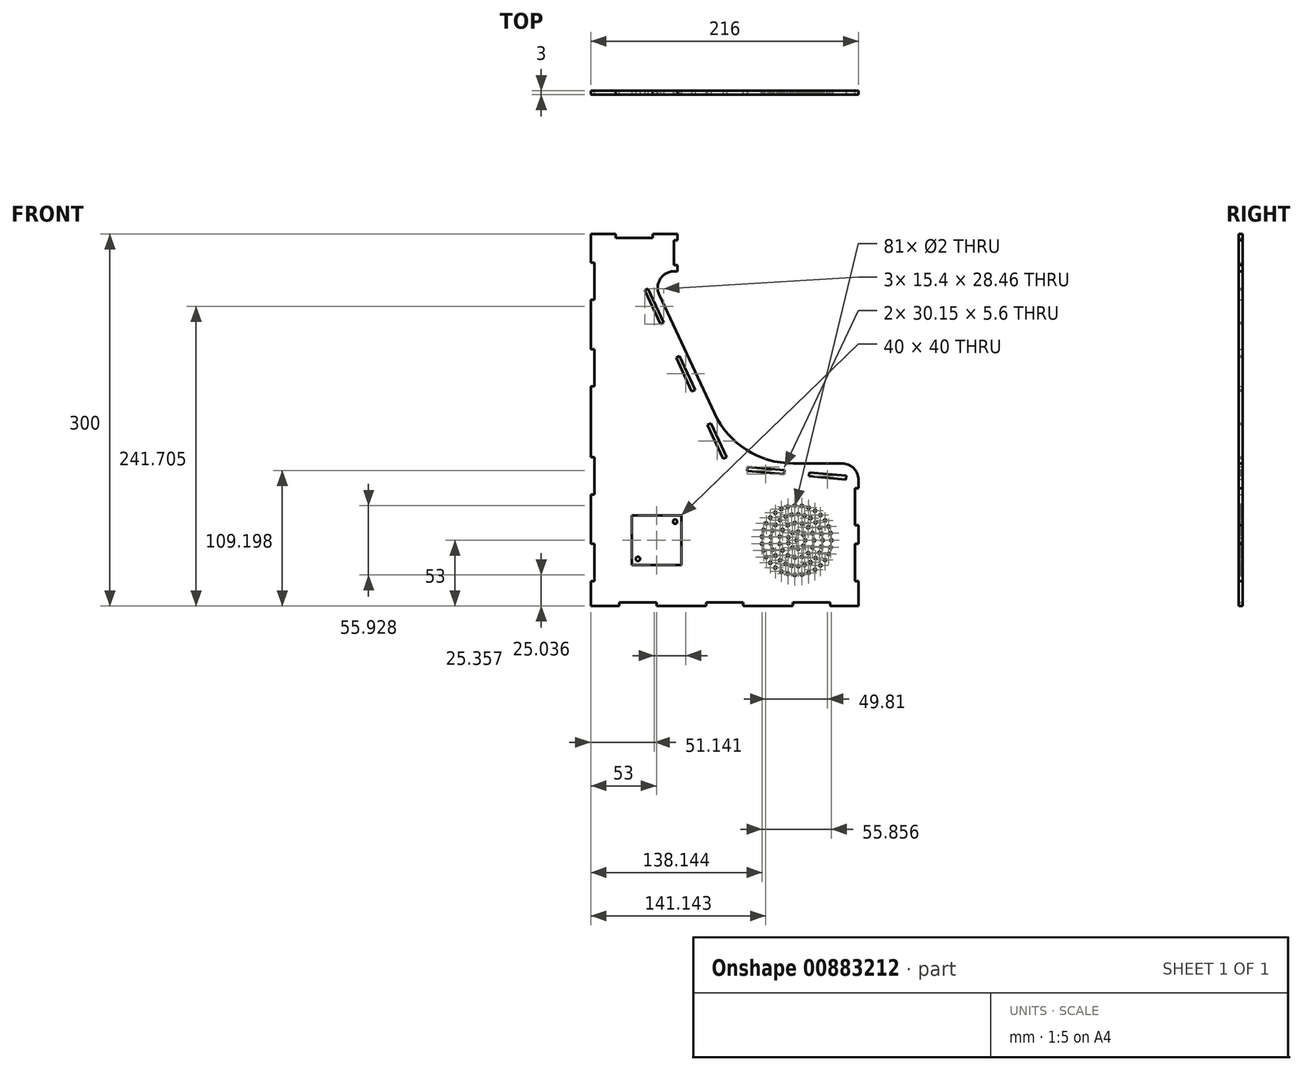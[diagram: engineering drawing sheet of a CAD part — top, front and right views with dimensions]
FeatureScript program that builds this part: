
annotation { "Feature Type Name" : "Feature", "Feature Type Description" : "" }
export const myFeature = defineFeature(function(context is Context, id is Id, definition is map)
    precondition{}
    {
        {
            var Q0;
            Q0=qCreatedBy(makeId("Front.planeOp"),FACE);
            var sketch = newSketch(context, id + "F0", { "sketchPlane" : qUnion([Q0])});
            skLineSegment(sketch, "E0", {"start": v(0, 0) * mm, "end": v(216, 0) * mm});
            skLineSegment(sketch, "E1", {"start": v(216, 0) * mm, "end": v(216, 115) * mm});
            skLineSegment(sketch, "E2", {"start": v(216, 115) * mm, "end": v(118.5, 115) * mm});
            skLineSegment(sketch, "E3", {"start": v(118.5, 115) * mm, "end": v(46.22, 270) * mm});
            skLineSegment(sketch, "E4", {"start": v(46.22, 270) * mm, "end": v(70, 270) * mm});
            skLineSegment(sketch, "E5", {"start": v(70, 270) * mm, "end": v(70, 300) * mm});
            skLineSegment(sketch, "E6", {"start": v(70, 300) * mm, "end": v(0, 300) * mm});
            skLineSegment(sketch, "E7", {"start": v(0, 300) * mm, "end": v(0, 0) * mm});
            skLineSegment(sketch, "E8", {"start": v(0, 277) * mm, "end": v(3, 277) * mm});
            skLineSegment(sketch, "E9", {"start": v(3, 277) * mm, "end": v(3, 247) * mm});
            skLineSegment(sketch, "E10", {"start": v(3, 247) * mm, "end": v(0, 247) * mm});
            skLineSegment(sketch, "E11", {"start": v(0, 207) * mm, "end": v(3, 207) * mm});
            skLineSegment(sketch, "E12", {"start": v(3, 207) * mm, "end": v(3, 177) * mm});
            skLineSegment(sketch, "E13", {"start": v(3, 177) * mm, "end": v(0, 177) * mm});
            skLineSegment(sketch, "E14", {"start": v(0, 120) * mm, "end": v(3, 120) * mm});
            skLineSegment(sketch, "E15", {"start": v(3, 120) * mm, "end": v(3, 90) * mm});
            skLineSegment(sketch, "E16", {"start": v(3, 90) * mm, "end": v(0, 90) * mm});
            skLineSegment(sketch, "E17", {"start": v(0, 50) * mm, "end": v(3, 50) * mm});
            skLineSegment(sketch, "E18", {"start": v(3, 50) * mm, "end": v(3, 20) * mm});
            skLineSegment(sketch, "E19", {"start": v(3, 20) * mm, "end": v(0, 20) * mm});
            skLineSegment(sketch, "E20", {"start": v(23, 0) * mm, "end": v(23, 3) * mm});
            skLineSegment(sketch, "E21", {"start": v(23, 3) * mm, "end": v(53, 3) * mm});
            skLineSegment(sketch, "E22", {"start": v(53, 3) * mm, "end": v(53, 0) * mm});
            skLineSegment(sketch, "E23", {"start": v(93, 0) * mm, "end": v(93, 3) * mm});
            skLineSegment(sketch, "E24", {"start": v(93, 3) * mm, "end": v(123, 3) * mm});
            skLineSegment(sketch, "E25", {"start": v(123, 3) * mm, "end": v(123, 0) * mm});
            skLineSegment(sketch, "E26", {"start": v(163, 0) * mm, "end": v(163, 3) * mm});
            skLineSegment(sketch, "E27", {"start": v(163, 3) * mm, "end": v(193, 3) * mm});
            skLineSegment(sketch, "E28", {"start": v(193, 3) * mm, "end": v(193, 0) * mm});
            skLineSegment(sketch, "E29", {"start": v(216, 20) * mm, "end": v(213, 20) * mm});
            skLineSegment(sketch, "E30", {"start": v(213, 20) * mm, "end": v(213, 50) * mm});
            skLineSegment(sketch, "E31", {"start": v(213, 50) * mm, "end": v(216, 50) * mm});
            skLineSegment(sketch, "E32", {"start": v(216, 65) * mm, "end": v(213, 65) * mm});
            skLineSegment(sketch, "E33", {"start": v(213, 65) * mm, "end": v(213, 95) * mm});
            skLineSegment(sketch, "E34", {"start": v(213, 95) * mm, "end": v(216, 95) * mm});
            skLineSegment(sketch, "E35", {"start": v(20, 300) * mm, "end": v(20, 297) * mm});
            skLineSegment(sketch, "E36", {"start": v(20, 297) * mm, "end": v(50, 297) * mm});
            skLineSegment(sketch, "E37", {"start": v(50, 297) * mm, "end": v(50, 300) * mm});
            skLineSegment(sketch, "E38", {"start": v(70, 295) * mm, "end": v(67, 295) * mm});
            skLineSegment(sketch, "E39", {"start": v(67, 295) * mm, "end": v(67, 275) * mm});
            skLineSegment(sketch, "E40", {"start": v(67, 275) * mm, "end": v(70, 275) * mm});
            skPoint(sketch, "E41", {"position": v(108, 3) * mm});
            skPoint(sketch, "E42", {"position": v(108, 0) * mm});
            skPoint(sketch, "E43", {"position": v(167.25, 115) * mm});
            skSolve(sketch);
        }
        {
            var Q0;
            {var subQ12=sQuery(id+"F0.wireOp",EDGE,"E2");Q0=makeQuery(id+"F0.imprint","IMPRINT",FACE,{"disambiguationData":[TD([[makeQuery(id+"F0.imprint","IMPRINT",EDGE,{"derivedFrom":subQ12}),1.0]])]});}
            var Q1;
            {var subQ0=sQuery(id+"F0.wireOp",EDGE,"E4");Q1=makeQuery(id+"F0.imprint","IMPRINT",FACE,{"disambiguationData":[TD([[makeQuery(id+"F0.imprint","IMPRINT",EDGE,{"derivedFrom":subQ0}),-1.0]])]});}
            var Q2;
            {var subQ3=sQuery(id+"F0.wireOp",EDGE,"8a221613-648f-4b06-892d-30c6be6bba23");Q2=makeQuery(id+"F0.imprint","IMPRINT",FACE,{"disambiguationData":[TD([[makeQuery(id+"F0.imprint","IMPRINT",EDGE,{"derivedFrom":subQ3}),-1.0]])]});}
            var Q3;
            {var subQ3=sQuery(id+"F0.wireOp",EDGE,"1dd4d70c-26e7-4ac6-b2af-ccda843abb65");Q3=makeQuery(id+"F0.imprint","IMPRINT",FACE,{"disambiguationData":[TD([[makeQuery(id+"F0.imprint","IMPRINT",EDGE,{"derivedFrom":subQ3}),1.0]])]});}
            extrude(context, id + "F1", {"entities" : qUnion([Q0, Q1, Q2, Q3]), "depth" : 3 * mm, "offsetDistance" : 25 * mm});
        }
        {
            var Q0;
            Q0=makeQuery(id+"F1.opExtrude","CAP_FACE",FACE,{"disambiguationData":[OSD([sQuery(id+"F0.wireOp",EDGE,"E0"),sQuery(id+"F0.wireOp",EDGE,"E1"),sQuery(id+"F0.wireOp",EDGE,"E2"),sQuery(id+"F0.wireOp",EDGE,"E3"),sQuery(id+"F0.wireOp",EDGE,"E4"),sQuery(id+"F0.wireOp",EDGE,"E5"),sQuery(id+"F0.wireOp",EDGE,"E6"),sQuery(id+"F0.wireOp",EDGE,"E7"),sQuery(id+"F0.wireOp",EDGE,"E8"),sQuery(id+"F0.wireOp",EDGE,"E9"),sQuery(id+"F0.wireOp",EDGE,"E10"),sQuery(id+"F0.wireOp",EDGE,"E11"),sQuery(id+"F0.wireOp",EDGE,"E12"),sQuery(id+"F0.wireOp",EDGE,"E13"),sQuery(id+"F0.wireOp",EDGE,"E14"),sQuery(id+"F0.wireOp",EDGE,"E15"),sQuery(id+"F0.wireOp",EDGE,"E16"),sQuery(id+"F0.wireOp",EDGE,"E17"),sQuery(id+"F0.wireOp",EDGE,"E18"),sQuery(id+"F0.wireOp",EDGE,"E19"),sQuery(id+"F0.wireOp",EDGE,"E20"),sQuery(id+"F0.wireOp",EDGE,"E21"),sQuery(id+"F0.wireOp",EDGE,"E22"),sQuery(id+"F0.wireOp",EDGE,"E23"),sQuery(id+"F0.wireOp",EDGE,"E24"),sQuery(id+"F0.wireOp",EDGE,"E25"),sQuery(id+"F0.wireOp",EDGE,"E26"),sQuery(id+"F0.wireOp",EDGE,"E27"),sQuery(id+"F0.wireOp",EDGE,"E28"),sQuery(id+"F0.wireOp",EDGE,"E29"),sQuery(id+"F0.wireOp",EDGE,"E30"),sQuery(id+"F0.wireOp",EDGE,"E31"),sQuery(id+"F0.wireOp",EDGE,"E32"),sQuery(id+"F0.wireOp",EDGE,"E33"),sQuery(id+"F0.wireOp",EDGE,"E34"),sQuery(id+"F0.wireOp",EDGE,"E35"),sQuery(id+"F0.wireOp",EDGE,"E36"),sQuery(id+"F0.wireOp",EDGE,"E37"),sQuery(id+"F0.wireOp",EDGE,"E38"),sQuery(id+"F0.wireOp",EDGE,"E39"),sQuery(id+"F0.wireOp",EDGE,"E40")])],"isStart":false});
            var sketch = newSketch(context, id + "F2", { "sketchPlane" : qUnion([Q0])});
            skLineSegment(sketch, "E44", {"start": v(0, 354.93) * mm, "end": v(177.98, -26.76) * mm, "construction": true});
            skLineSegment(sketch, "E45", {"start": v(3, 122.8) * mm, "end": v(213, 104.42) * mm, "construction": true});
            skLineSegment(sketch, "E46", {"start": v(126.33, 112) * mm, "end": v(156.22, 109.39) * mm});
            skLineSegment(sketch, "E47", {"start": v(156.22, 109.39) * mm, "end": v(155.96, 106.4) * mm});
            skLineSegment(sketch, "E48", {"start": v(155.96, 106.4) * mm, "end": v(126.07, 109.01) * mm});
            skLineSegment(sketch, "E49", {"start": v(126.07, 109.01) * mm, "end": v(126.33, 112) * mm});
            skLineSegment(sketch, "E50", {"start": v(176.14, 107.64) * mm, "end": v(175.88, 104.65) * mm});
            skLineSegment(sketch, "E51", {"start": v(175.88, 104.65) * mm, "end": v(205.77, 102.04) * mm});
            skLineSegment(sketch, "E52", {"start": v(205.77, 102.04) * mm, "end": v(206.03, 105.03) * mm});
            skLineSegment(sketch, "E53", {"start": v(206.03, 105.03) * mm, "end": v(176.14, 107.64) * mm});
            skLineSegment(sketch, "E54", {"start": v(71.52, 201.56) * mm, "end": v(68.8, 200.29) * mm});
            skLineSegment(sketch, "E55", {"start": v(68.8, 200.29) * mm, "end": v(81.48, 173.1) * mm});
            skLineSegment(sketch, "E56", {"start": v(81.48, 173.1) * mm, "end": v(84.2, 174.37) * mm});
            skLineSegment(sketch, "E57", {"start": v(84.2, 174.37) * mm, "end": v(71.52, 201.56) * mm});
            skLineSegment(sketch, "E58", {"start": v(96.88, 147.18) * mm, "end": v(94.16, 145.9) * mm});
            skLineSegment(sketch, "E59", {"start": v(94.16, 145.9) * mm, "end": v(106.83, 118.72) * mm});
            skLineSegment(sketch, "E60", {"start": v(106.83, 118.72) * mm, "end": v(109.55, 119.99) * mm});
            skLineSegment(sketch, "E61", {"start": v(109.55, 119.99) * mm, "end": v(96.88, 147.18) * mm});
            skPoint(sketch, "E62", {"position": v(112.72, 113.2) * mm});
            skLineSegment(sketch, "E63", {"start": v(58.84, 228.74) * mm, "end": v(46.16, 255.93) * mm});
            skLineSegment(sketch, "E64", {"start": v(46.16, 255.93) * mm, "end": v(43.44, 254.67) * mm});
            skLineSegment(sketch, "E65", {"start": v(43.44, 254.67) * mm, "end": v(56.12, 227.48) * mm});
            skLineSegment(sketch, "E66", {"start": v(56.12, 227.48) * mm, "end": v(58.84, 228.74) * mm});
            skCircle(sketch, "E67", {"center": v(53, 53) * mm, "radius": 5 * mm});
            skLineSegment(sketch, "E68.bottom", {"start": v(73, 73) * mm, "end": v(33, 73) * mm});
            skLineSegment(sketch, "E68.top", {"start": v(73, 33) * mm, "end": v(33, 33) * mm});
            skLineSegment(sketch, "E68.left", {"start": v(73, 73) * mm, "end": v(73, 33) * mm});
            skLineSegment(sketch, "E68.right", {"start": v(33, 73) * mm, "end": v(33, 33) * mm});
            skCircle(sketch, "E69", {"center": v(38, 68) * mm, "radius": 1.75 * mm});
            skCircle(sketch, "E70.MirrorC", {"center": v(68, 68) * mm, "radius": 1.75 * mm});
            skCircle(sketch, "E71.MirrorC", {"center": v(68, 38) * mm, "radius": 1.75 * mm});
            skCircle(sketch, "E72.MirrorC", {"center": v(38, 38) * mm, "radius": 1.75 * mm});
            skSolve(sketch);
        }
        {
            var Q0;
            Q0=makeQuery(id+"F2.imprint","IMPRINT",FACE,{"disambiguationData":[TD([[makeQuery(id+"F2.imprint","IMPRINT",EDGE,{"derivedFrom":sQuery(id+"F2.wireOp",EDGE,"E46")}),-1.0]])]});
            var Q1;
            Q1=makeQuery(id+"F2.imprint","IMPRINT",FACE,{"disambiguationData":[TD([[makeQuery(id+"F2.imprint","IMPRINT",EDGE,{"derivedFrom":sQuery(id+"F2.wireOp",EDGE,"E50")}),1.0]])]});
            var Q2;
            Q2=makeQuery(id+"F2.imprint","IMPRINT",FACE,{"disambiguationData":[TD([[makeQuery(id+"F2.imprint","IMPRINT",EDGE,{"derivedFrom":sQuery(id+"F2.wireOp",EDGE,"E54")}),1.0]])]});
            var Q3;
            Q3=makeQuery(id+"F2.imprint","IMPRINT",FACE,{"disambiguationData":[TD([[makeQuery(id+"F2.imprint","IMPRINT",EDGE,{"derivedFrom":sQuery(id+"F2.wireOp",EDGE,"E58")}),1.0]])]});
            var Q4;
            Q4=makeQuery(id+"F2.imprint","IMPRINT",FACE,{"disambiguationData":[TD([[makeQuery(id+"F2.imprint","IMPRINT",EDGE,{"derivedFrom":sQuery(id+"F2.wireOp",EDGE,"E63")}),1.0]])]});
            var Q5;
            Q5=makeQuery(id+"F2.imprint","IMPRINT",FACE,{"disambiguationData":[TD([[makeQuery(id+"F2.imprint","IMPRINT",EDGE,{"derivedFrom":sQuery(id+"F2.wireOp",EDGE,"E69")}),1.0]])]});
            var Q6;
            Q6=makeQuery(id+"F2.imprint","IMPRINT",FACE,{"disambiguationData":[TD([[makeQuery(id+"F2.imprint","IMPRINT",EDGE,{"derivedFrom":sQuery(id+"F2.wireOp",EDGE,"E67")}),1.0]])]});
            var Q7;
            Q7=makeQuery(id+"F2.imprint","IMPRINT",FACE,{"disambiguationData":[TD([[makeQuery(id+"F2.imprint","IMPRINT",EDGE,{"derivedFrom":sQuery(id+"F2.wireOp",EDGE,"E70.MirrorC")}),-1.0]])]});
            var Q8;
            Q8=makeQuery(id+"F2.imprint","IMPRINT",FACE,{"disambiguationData":[TD([[makeQuery(id+"F2.imprint","IMPRINT",EDGE,{"derivedFrom":sQuery(id+"F2.wireOp",EDGE,"E71.MirrorC")}),1.0]])]});
            var Q9;
            Q9=makeQuery(id+"F2.imprint","IMPRINT",FACE,{"disambiguationData":[TD([[makeQuery(id+"F2.imprint","IMPRINT",EDGE,{"derivedFrom":sQuery(id+"F2.wireOp",EDGE,"E72.MirrorC")}),-1.0]])]});
            var Q10;
            Q10=makeQuery(id+"F1.opExtrude","CAP_FACE",FACE,{"disambiguationData":[OSD([sQuery(id+"F0.wireOp",EDGE,"E0"),sQuery(id+"F0.wireOp",EDGE,"E1"),sQuery(id+"F0.wireOp",EDGE,"E2"),sQuery(id+"F0.wireOp",EDGE,"E3"),sQuery(id+"F0.wireOp",EDGE,"E4"),sQuery(id+"F0.wireOp",EDGE,"E5"),sQuery(id+"F0.wireOp",EDGE,"E6"),sQuery(id+"F0.wireOp",EDGE,"E7"),sQuery(id+"F0.wireOp",EDGE,"E8"),sQuery(id+"F0.wireOp",EDGE,"E9"),sQuery(id+"F0.wireOp",EDGE,"E10"),sQuery(id+"F0.wireOp",EDGE,"E11"),sQuery(id+"F0.wireOp",EDGE,"E12"),sQuery(id+"F0.wireOp",EDGE,"E13"),sQuery(id+"F0.wireOp",EDGE,"E14"),sQuery(id+"F0.wireOp",EDGE,"E15"),sQuery(id+"F0.wireOp",EDGE,"E16"),sQuery(id+"F0.wireOp",EDGE,"E17"),sQuery(id+"F0.wireOp",EDGE,"E18"),sQuery(id+"F0.wireOp",EDGE,"E19"),sQuery(id+"F0.wireOp",EDGE,"E20"),sQuery(id+"F0.wireOp",EDGE,"E21"),sQuery(id+"F0.wireOp",EDGE,"E22"),sQuery(id+"F0.wireOp",EDGE,"E23"),sQuery(id+"F0.wireOp",EDGE,"E24"),sQuery(id+"F0.wireOp",EDGE,"E25"),sQuery(id+"F0.wireOp",EDGE,"E26"),sQuery(id+"F0.wireOp",EDGE,"E27"),sQuery(id+"F0.wireOp",EDGE,"E28"),sQuery(id+"F0.wireOp",EDGE,"E29"),sQuery(id+"F0.wireOp",EDGE,"E30"),sQuery(id+"F0.wireOp",EDGE,"E31"),sQuery(id+"F0.wireOp",EDGE,"E32"),sQuery(id+"F0.wireOp",EDGE,"E33"),sQuery(id+"F0.wireOp",EDGE,"E34"),sQuery(id+"F0.wireOp",EDGE,"E35"),sQuery(id+"F0.wireOp",EDGE,"E36"),sQuery(id+"F0.wireOp",EDGE,"E37"),sQuery(id+"F0.wireOp",EDGE,"E38"),sQuery(id+"F0.wireOp",EDGE,"E39"),sQuery(id+"F0.wireOp",EDGE,"E40")])],"isStart":true});
            extrude(context, id + "F3", {"entities" : qUnion([Q0, Q1, Q2, Q3, Q4, Q5, Q6, Q7, Q8, Q9]), "operationType" : NewBodyOperationType.REMOVE, "endBound" : BoundingType.UP_TO_SURFACE, "oppositeDirection" : true, "depth" : 25 * mm, "endBoundEntityFace" : qUnion([Q10]), "offsetDistance" : 25 * mm});
        }
        {
            var Q0;
            Q0=makeQuery(id+"F1.opExtrude","SWEPT_EDGE",EDGE,{"disambiguationData":[OSD([sQuery(id+"F0.wireOp",EDGE,"E1"),sQuery(id+"F0.wireOp",EDGE,"E2")])]});
            var Q1;
            Q1=makeQuery(id+"F1.opExtrude","SWEPT_EDGE",EDGE,{"disambiguationData":[OSD([sQuery(id+"F0.wireOp",EDGE,"E3"),sQuery(id+"F0.wireOp",EDGE,"E4")])]});
            fillet(context, id + "F4", {"entities" : qUnion([Q0, Q1]), "radius" : 13.5 * mm, "tangentPropagation" : true, "allowEdgeOverflow" : false});
        }
        {
            var Q0;
            Q0=makeQuery(id+"F1.opExtrude","SWEPT_EDGE",EDGE,{"disambiguationData":[OSD([sQuery(id+"F0.wireOp",EDGE,"E2"),sQuery(id+"F0.wireOp",EDGE,"E3")])]});
            fillet(context, id + "F5", {"entities" : qUnion([Q0]), "radius" : 70 * mm, "tangentPropagation" : true, "allowEdgeOverflow" : false});
        }
        {
            var Q0;
            Q0=makeQuery(id+"F1.opExtrude","CAP_FACE",FACE,{"disambiguationData":[OSD([sQuery(id+"F0.wireOp",EDGE,"E0"),sQuery(id+"F0.wireOp",EDGE,"E1"),sQuery(id+"F0.wireOp",EDGE,"E2"),sQuery(id+"F0.wireOp",EDGE,"E3"),sQuery(id+"F0.wireOp",EDGE,"E4"),sQuery(id+"F0.wireOp",EDGE,"E5"),sQuery(id+"F0.wireOp",EDGE,"E6"),sQuery(id+"F0.wireOp",EDGE,"E7"),sQuery(id+"F0.wireOp",EDGE,"E8"),sQuery(id+"F0.wireOp",EDGE,"E9"),sQuery(id+"F0.wireOp",EDGE,"E10"),sQuery(id+"F0.wireOp",EDGE,"E11"),sQuery(id+"F0.wireOp",EDGE,"E12"),sQuery(id+"F0.wireOp",EDGE,"E13"),sQuery(id+"F0.wireOp",EDGE,"E14"),sQuery(id+"F0.wireOp",EDGE,"E15"),sQuery(id+"F0.wireOp",EDGE,"E16"),sQuery(id+"F0.wireOp",EDGE,"E17"),sQuery(id+"F0.wireOp",EDGE,"E18"),sQuery(id+"F0.wireOp",EDGE,"E19"),sQuery(id+"F0.wireOp",EDGE,"E20"),sQuery(id+"F0.wireOp",EDGE,"E21"),sQuery(id+"F0.wireOp",EDGE,"E22"),sQuery(id+"F0.wireOp",EDGE,"E23"),sQuery(id+"F0.wireOp",EDGE,"E24"),sQuery(id+"F0.wireOp",EDGE,"E25"),sQuery(id+"F0.wireOp",EDGE,"E26"),sQuery(id+"F0.wireOp",EDGE,"E27"),sQuery(id+"F0.wireOp",EDGE,"E28"),sQuery(id+"F0.wireOp",EDGE,"E29"),sQuery(id+"F0.wireOp",EDGE,"E30"),sQuery(id+"F0.wireOp",EDGE,"E31"),sQuery(id+"F0.wireOp",EDGE,"E32"),sQuery(id+"F0.wireOp",EDGE,"E33"),sQuery(id+"F0.wireOp",EDGE,"E34"),sQuery(id+"F0.wireOp",EDGE,"E35"),sQuery(id+"F0.wireOp",EDGE,"E36"),sQuery(id+"F0.wireOp",EDGE,"E37"),sQuery(id+"F0.wireOp",EDGE,"E38"),sQuery(id+"F0.wireOp",EDGE,"E39"),sQuery(id+"F0.wireOp",EDGE,"E40")])],"isStart":false});
            var sketch = newSketch(context, id + "F6", { "sketchPlane" : qUnion([Q0])});
            skCircle(sketch, "E73", {"center": v(166, 53) * mm, "radius": 1 * mm});
            skCircle(sketch, "E74", {"center": v(173, 53) * mm, "radius": 1 * mm});
            skCircle(sketch, "E75", {"center": v(180, 53) * mm, "radius": 1 * mm});
            skCircle(sketch, "E76", {"center": v(187, 53) * mm, "radius": 1 * mm});
            skCircle(sketch, "E77.1.0", {"center": v(171.36, 57.5) * mm, "radius": 1 * mm});
            skCircle(sketch, "E77.2.0", {"center": v(167.22, 59.9) * mm, "radius": 1 * mm});
            skCircle(sketch, "E77.3.0", {"center": v(162.5, 59.06) * mm, "radius": 1 * mm});
            skCircle(sketch, "E77.4.0", {"center": v(159.42, 55.4) * mm, "radius": 1 * mm});
            skCircle(sketch, "E77.5.0", {"center": v(159.42, 50.6) * mm, "radius": 1 * mm});
            skCircle(sketch, "E77.6.0", {"center": v(162.5, 46.94) * mm, "radius": 1 * mm});
            skCircle(sketch, "E77.7.0", {"center": v(167.22, 46.1) * mm, "radius": 1 * mm});
            skCircle(sketch, "E78.1.0", {"center": v(178.79, 58.7) * mm, "radius": 1 * mm});
            skCircle(sketch, "E78.2.0", {"center": v(175.37, 63.4) * mm, "radius": 1 * mm});
            skCircle(sketch, "E78.3.0", {"center": v(170.33, 66.31) * mm, "radius": 1 * mm});
            skCircle(sketch, "E78.4.0", {"center": v(164.54, 66.92) * mm, "radius": 1 * mm});
            skCircle(sketch, "E78.5.0", {"center": v(159, 65.12) * mm, "radius": 1 * mm});
            skCircle(sketch, "E78.6.0", {"center": v(154.67, 61.23) * mm, "radius": 1 * mm});
            skCircle(sketch, "E78.7.0", {"center": v(152.3, 55.91) * mm, "radius": 1 * mm});
            skCircle(sketch, "E78.8.0", {"center": v(152.3, 50.09) * mm, "radius": 1 * mm});
            skCircle(sketch, "E78.9.0", {"center": v(154.67, 44.77) * mm, "radius": 1 * mm});
            skCircle(sketch, "E78.10.0", {"center": v(159, 40.88) * mm, "radius": 1 * mm});
            skCircle(sketch, "E78.11.0", {"center": v(164.54, 39.08) * mm, "radius": 1 * mm});
            skCircle(sketch, "E78.12.0", {"center": v(170.33, 39.69) * mm, "radius": 1 * mm});
            skCircle(sketch, "E78.13.0", {"center": v(175.37, 42.6) * mm, "radius": 1 * mm});
            skCircle(sketch, "E78.14.0", {"center": v(178.79, 47.3) * mm, "radius": 1 * mm});
            skCircle(sketch, "E79.1.0", {"center": v(186.34, 58.22) * mm, "radius": 1 * mm});
            skCircle(sketch, "E79.2.0", {"center": v(184.4, 63.12) * mm, "radius": 1 * mm});
            skCircle(sketch, "E79.3.0", {"center": v(181.3, 67.38) * mm, "radius": 1 * mm});
            skCircle(sketch, "E79.4.0", {"center": v(177.25, 70.73) * mm, "radius": 1 * mm});
            skCircle(sketch, "E79.5.0", {"center": v(172.49, 72.97) * mm, "radius": 1 * mm});
            skCircle(sketch, "E79.6.0", {"center": v(167.32, 73.96) * mm, "radius": 1 * mm});
            skCircle(sketch, "E79.7.0", {"center": v(162.06, 73.63) * mm, "radius": 1 * mm});
            skCircle(sketch, "E79.8.0", {"center": v(157.06, 72) * mm, "radius": 1 * mm});
            skCircle(sketch, "E79.9.0", {"center": v(152.61, 69.18) * mm, "radius": 1 * mm});
            skCircle(sketch, "E79.10.0", {"center": v(149.01, 65.34) * mm, "radius": 1 * mm});
            skCircle(sketch, "E79.11.0", {"center": v(146.47, 60.73) * mm, "radius": 1 * mm});
            skCircle(sketch, "E79.12.0", {"center": v(145.17, 55.63) * mm, "radius": 1 * mm});
            skCircle(sketch, "E79.13.0", {"center": v(145.17, 50.37) * mm, "radius": 1 * mm});
            skCircle(sketch, "E79.14.0", {"center": v(146.47, 45.27) * mm, "radius": 1 * mm});
            skCircle(sketch, "E79.15.0", {"center": v(149.01, 40.66) * mm, "radius": 1 * mm});
            skCircle(sketch, "E79.16.0", {"center": v(152.61, 36.82) * mm, "radius": 1 * mm});
            skCircle(sketch, "E79.17.0", {"center": v(157.06, 34) * mm, "radius": 1 * mm});
            skCircle(sketch, "E79.18.0", {"center": v(162.06, 32.37) * mm, "radius": 1 * mm});
            skCircle(sketch, "E79.19.0", {"center": v(167.32, 32.04) * mm, "radius": 1 * mm});
            skCircle(sketch, "E79.20.0", {"center": v(172.49, 33.03) * mm, "radius": 1 * mm});
            skCircle(sketch, "E79.21.0", {"center": v(177.25, 35.27) * mm, "radius": 1 * mm});
            skCircle(sketch, "E79.22.0", {"center": v(181.3, 38.62) * mm, "radius": 1 * mm});
            skCircle(sketch, "E79.23.0", {"center": v(184.4, 42.88) * mm, "radius": 1 * mm});
            skCircle(sketch, "E79.24.0", {"center": v(186.34, 47.78) * mm, "radius": 1 * mm});
            skCircle(sketch, "E80", {"center": v(194, 53) * mm, "radius": 1 * mm});
            skCircle(sketch, "E81.1.0", {"center": v(193.43, 58.64) * mm, "radius": 1 * mm});
            skCircle(sketch, "E81.2.0", {"center": v(191.73, 64.04) * mm, "radius": 1 * mm});
            skCircle(sketch, "E81.3.0", {"center": v(188.98, 69) * mm, "radius": 1 * mm});
            skCircle(sketch, "E81.4.0", {"center": v(185.3, 73.3) * mm, "radius": 1 * mm});
            skCircle(sketch, "E81.5.0", {"center": v(180.81, 76.76) * mm, "radius": 1 * mm});
            skCircle(sketch, "E81.6.0", {"center": v(175.72, 79.26) * mm, "radius": 1 * mm});
            skCircle(sketch, "E81.7.0", {"center": v(170.24, 80.68) * mm, "radius": 1 * mm});
            skCircle(sketch, "E81.8.0", {"center": v(164.58, 80.96) * mm, "radius": 1 * mm});
            skCircle(sketch, "E81.9.0", {"center": v(158.98, 80.1) * mm, "radius": 1 * mm});
            skCircle(sketch, "E81.10.0", {"center": v(153.67, 78.14) * mm, "radius": 1 * mm});
            skCircle(sketch, "E81.11.0", {"center": v(148.86, 75.14) * mm, "radius": 1 * mm});
            skCircle(sketch, "E81.12.0", {"center": v(144.75, 71.24) * mm, "radius": 1 * mm});
            skCircle(sketch, "E81.13.0", {"center": v(141.52, 66.59) * mm, "radius": 1 * mm});
            skCircle(sketch, "E81.14.0", {"center": v(139.28, 61.38) * mm, "radius": 1 * mm});
            skCircle(sketch, "E81.15.0", {"center": v(138.14, 55.83) * mm, "radius": 1 * mm});
            skCircle(sketch, "E81.16.0", {"center": v(138.14, 50.17) * mm, "radius": 1 * mm});
            skCircle(sketch, "E81.17.0", {"center": v(139.28, 44.62) * mm, "radius": 1 * mm});
            skCircle(sketch, "E81.18.0", {"center": v(141.52, 39.41) * mm, "radius": 1 * mm});
            skCircle(sketch, "E81.19.0", {"center": v(144.75, 34.76) * mm, "radius": 1 * mm});
            skCircle(sketch, "E81.20.0", {"center": v(148.86, 30.86) * mm, "radius": 1 * mm});
            skCircle(sketch, "E81.21.0", {"center": v(153.67, 27.86) * mm, "radius": 1 * mm});
            skCircle(sketch, "E81.22.0", {"center": v(158.98, 25.9) * mm, "radius": 1 * mm});
            skCircle(sketch, "E81.23.0", {"center": v(164.58, 25.04) * mm, "radius": 1 * mm});
            skCircle(sketch, "E81.24.0", {"center": v(170.24, 25.32) * mm, "radius": 1 * mm});
            skCircle(sketch, "E81.25.0", {"center": v(175.72, 26.74) * mm, "radius": 1 * mm});
            skCircle(sketch, "E81.26.0", {"center": v(180.81, 29.24) * mm, "radius": 1 * mm});
            skCircle(sketch, "E81.27.0", {"center": v(185.3, 32.7) * mm, "radius": 1 * mm});
            skCircle(sketch, "E81.28.0", {"center": v(188.98, 37) * mm, "radius": 1 * mm});
            skCircle(sketch, "E81.29.0", {"center": v(191.73, 41.96) * mm, "radius": 1 * mm});
            skCircle(sketch, "E81.30.0", {"center": v(193.43, 47.36) * mm, "radius": 1 * mm});
            skCircle(sketch, "E82.1.8.0", {"center": v(171.36, 48.5) * mm, "radius": 1 * mm});
            skSolve(sketch);
        }
        {
            var Q0;
            Q0=qSketchRegion(id+"F6",true);
            var Q1;
            Q1=makeQuery(id+"F1.opExtrude","CAP_FACE",FACE,{"disambiguationData":[OSD([sQuery(id+"F0.wireOp",EDGE,"E0"),sQuery(id+"F0.wireOp",EDGE,"E1"),sQuery(id+"F0.wireOp",EDGE,"E2"),sQuery(id+"F0.wireOp",EDGE,"E3"),sQuery(id+"F0.wireOp",EDGE,"E4"),sQuery(id+"F0.wireOp",EDGE,"E5"),sQuery(id+"F0.wireOp",EDGE,"E6"),sQuery(id+"F0.wireOp",EDGE,"E7"),sQuery(id+"F0.wireOp",EDGE,"E8"),sQuery(id+"F0.wireOp",EDGE,"E9"),sQuery(id+"F0.wireOp",EDGE,"E10"),sQuery(id+"F0.wireOp",EDGE,"E11"),sQuery(id+"F0.wireOp",EDGE,"E12"),sQuery(id+"F0.wireOp",EDGE,"E13"),sQuery(id+"F0.wireOp",EDGE,"E14"),sQuery(id+"F0.wireOp",EDGE,"E15"),sQuery(id+"F0.wireOp",EDGE,"E16"),sQuery(id+"F0.wireOp",EDGE,"E17"),sQuery(id+"F0.wireOp",EDGE,"E18"),sQuery(id+"F0.wireOp",EDGE,"E19"),sQuery(id+"F0.wireOp",EDGE,"E20"),sQuery(id+"F0.wireOp",EDGE,"E21"),sQuery(id+"F0.wireOp",EDGE,"E22"),sQuery(id+"F0.wireOp",EDGE,"E23"),sQuery(id+"F0.wireOp",EDGE,"E24"),sQuery(id+"F0.wireOp",EDGE,"E25"),sQuery(id+"F0.wireOp",EDGE,"E26"),sQuery(id+"F0.wireOp",EDGE,"E27"),sQuery(id+"F0.wireOp",EDGE,"E28"),sQuery(id+"F0.wireOp",EDGE,"E29"),sQuery(id+"F0.wireOp",EDGE,"E30"),sQuery(id+"F0.wireOp",EDGE,"E31"),sQuery(id+"F0.wireOp",EDGE,"E32"),sQuery(id+"F0.wireOp",EDGE,"E33"),sQuery(id+"F0.wireOp",EDGE,"E34"),sQuery(id+"F0.wireOp",EDGE,"E35"),sQuery(id+"F0.wireOp",EDGE,"E36"),sQuery(id+"F0.wireOp",EDGE,"E37"),sQuery(id+"F0.wireOp",EDGE,"E38"),sQuery(id+"F0.wireOp",EDGE,"E39"),sQuery(id+"F0.wireOp",EDGE,"E40")])],"isStart":true});
            extrude(context, id + "F7", {"entities" : qUnion([Q0]), "operationType" : NewBodyOperationType.REMOVE, "endBound" : BoundingType.UP_TO_SURFACE, "oppositeDirection" : true, "depth" : 25 * mm, "endBoundEntityFace" : qUnion([Q1]), "offsetDistance" : 25 * mm});
        }
    });
